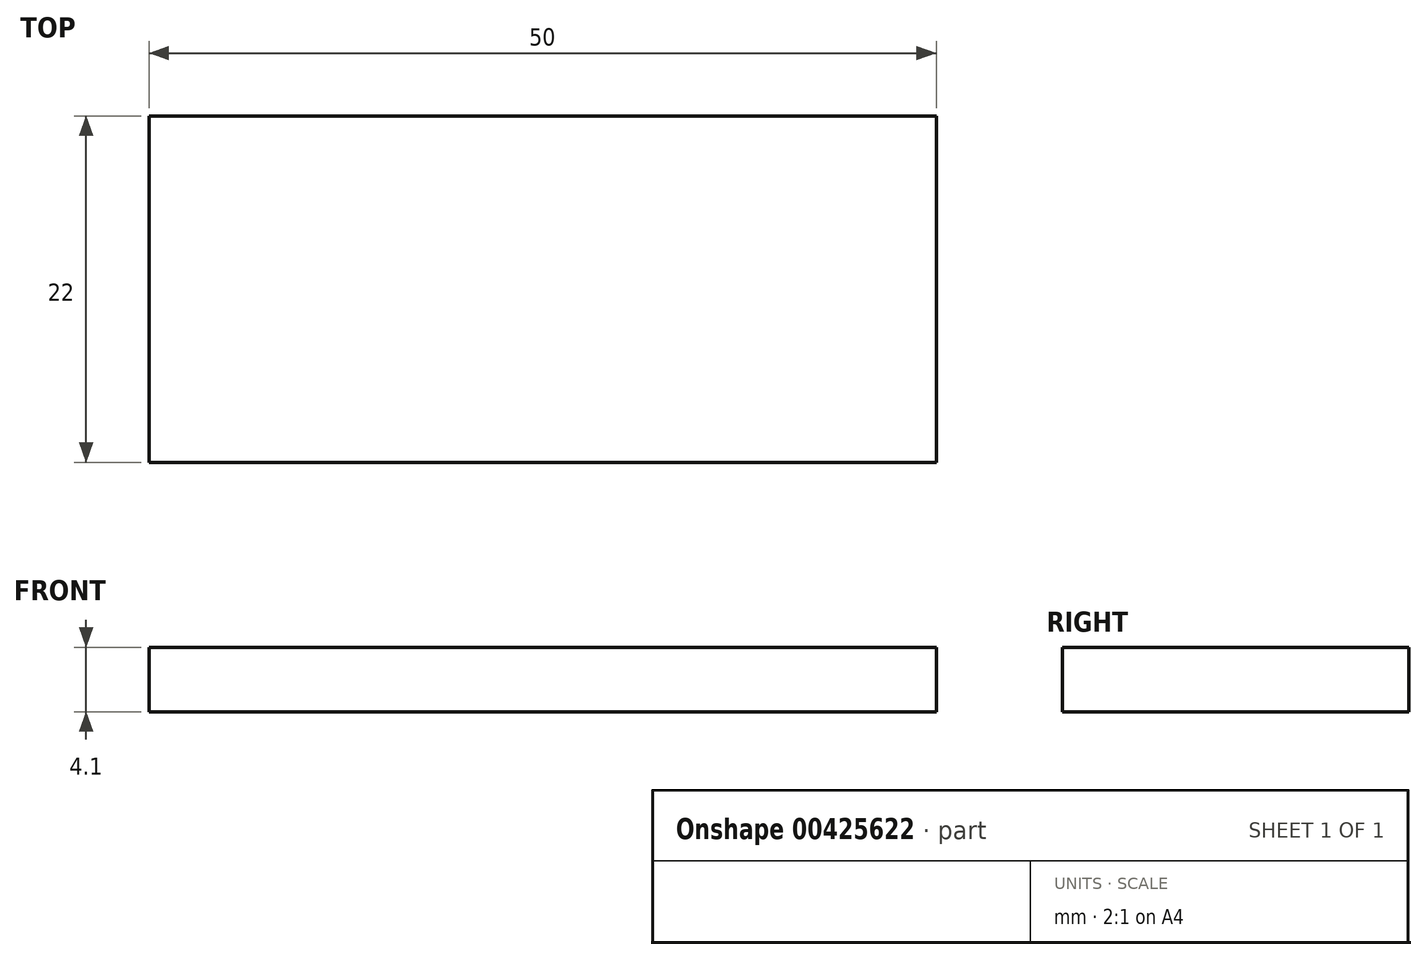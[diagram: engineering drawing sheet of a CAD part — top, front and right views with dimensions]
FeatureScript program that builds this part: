
annotation { "Feature Type Name" : "Feature", "Feature Type Description" : "" }
export const myFeature = defineFeature(function(context is Context, id is Id, definition is map)
    precondition{}
    {
        {
            var Q0;
            Q0=qCreatedBy(makeId("Top.planeOp"),FACE);
            var sketch = newSketch(context, id + "F0", { "sketchPlane" : qUnion([Q0])});
            skLineSegment(sketch, "E0.bottom", {"start": v(25, -11) * mm, "end": v(-25, -11) * mm});
            skLineSegment(sketch, "E0.top", {"start": v(25, 11) * mm, "end": v(-25, 11) * mm});
            skLineSegment(sketch, "E0.left", {"start": v(25, -11) * mm, "end": v(25, 11) * mm});
            skLineSegment(sketch, "E0.right", {"start": v(-25, -11) * mm, "end": v(-25, 11) * mm});
            skPoint(sketch, "E0.middle", {"position": v(0, 0) * mm});
            skSolve(sketch);
        }
        {
            var Q0;
            Q0=makeQuery(id+"F0.imprint","IMPRINT",FACE,{"disambiguationData":[TD([[makeQuery(id+"F0.imprint","IMPRINT",EDGE,{"derivedFrom":sQuery(id+"F0.wireOp",EDGE,"E0.bottom")}),-1.0]])]});
            extrude(context, id + "F1", {"entities" : qUnion([Q0]), "oppositeDirection" : true, "depth" : 4.1 * mm, "offsetDistance" : 25 * mm});
        }
    });
